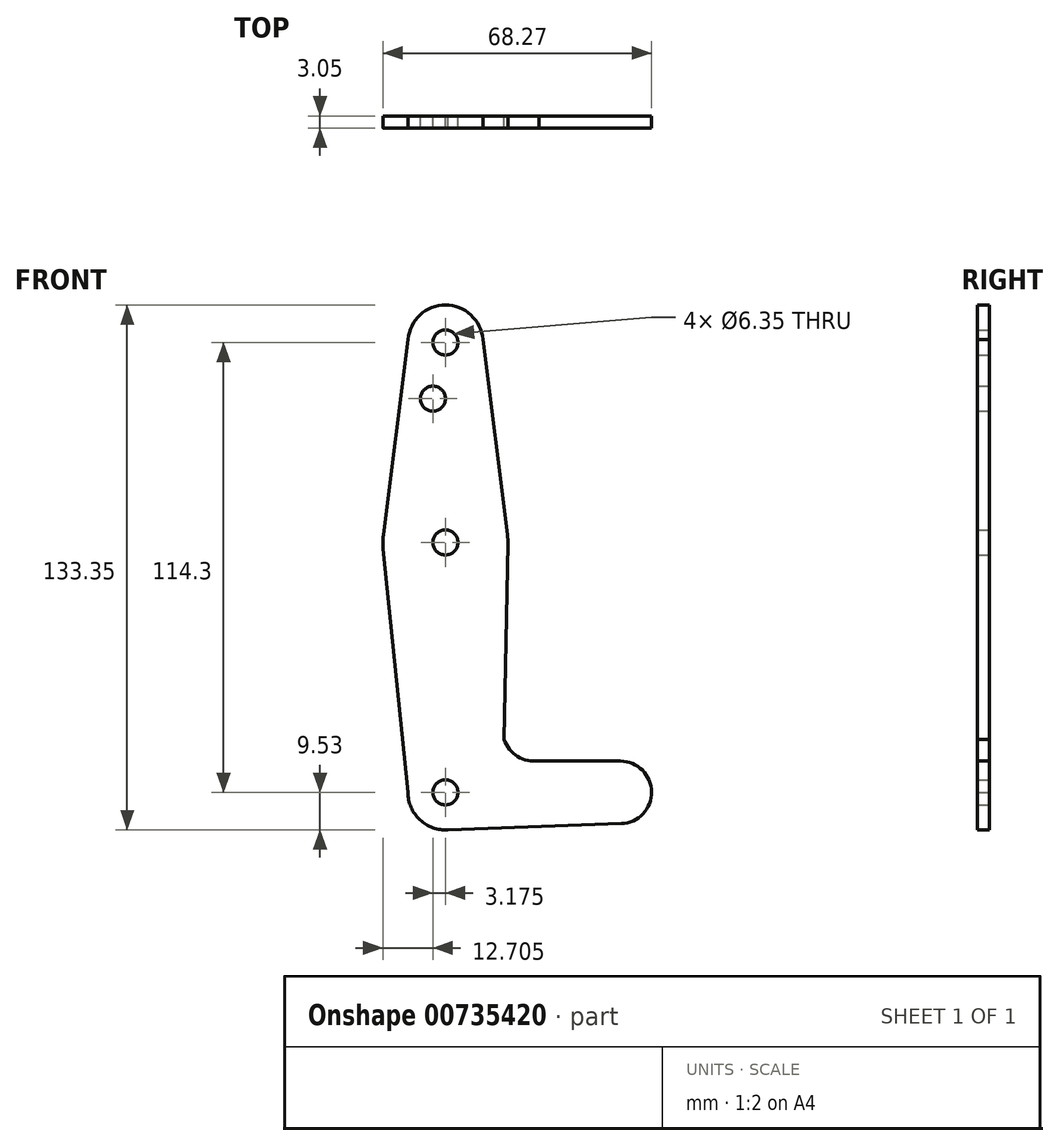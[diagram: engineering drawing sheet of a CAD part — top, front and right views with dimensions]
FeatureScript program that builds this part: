
annotation { "Feature Type Name" : "Feature", "Feature Type Description" : "" }
export const myFeature = defineFeature(function(context is Context, id is Id, definition is map)
    precondition{}
    {
        {
            var Q0;
            Q0=qCreatedBy(makeId("Front.planeOp"),FACE);
            var sketch = newSketch(context, id + "F0", { "sketchPlane" : qUnion([Q0])});
            skCircle(sketch, "E0", {"center": v(0, 0) * mm, "radius": 9.53 * mm});
            skLineSegment(sketch, "E1", {"start": v(0, 0) * mm, "end": v(0, 63.5) * mm});
            skCircle(sketch, "E2", {"center": v(0, 63.5) * mm, "radius": 15.88 * mm});
            skLineSegment(sketch, "E3", {"start": v(0, 63.5) * mm, "end": v(0, 114.3) * mm});
            skCircle(sketch, "E4", {"center": v(0, 114.3) * mm, "radius": 9.53 * mm});
            skLineSegment(sketch, "E5", {"start": v(0, 0) * mm, "end": v(44.45, 0) * mm});
            skCircle(sketch, "E6", {"center": v(44.45, 0) * mm, "radius": 7.94 * mm});
            skCircle(sketch, "E7", {"center": v(0, 114.3) * mm, "radius": 3.18 * mm});
            skCircle(sketch, "E8", {"center": v(0, 0) * mm, "radius": 3.18 * mm});
            skLineSegment(sketch, "E9", {"start": v(-9.4, 115.89) * mm, "end": v(-15.75, 65.49) * mm});
            skLineSegment(sketch, "E10", {"start": v(9.4, 115.89) * mm, "end": v(15.75, 65.49) * mm});
            skCircle(sketch, "E11", {"center": v(0, 63.5) * mm, "radius": 3.18 * mm});
            skCircle(sketch, "E12", {"center": v(-3.18, 100.03) * mm, "radius": 3.18 * mm});
            skLineSegment(sketch, "E13", {"start": v(0, -9.53) * mm, "end": v(44.73, -7.93) * mm});
            skLineSegment(sketch, "E14", {"start": v(15.87, 63.2) * mm, "end": v(14.94, 13.46) * mm});
            skArc(sketch, "E15", {"start": v(14.94, 13.46) * mm, "mid": v(18.36, 9.1) * mm, "end": v(23.8, 8.04) * mm});
            skLineSegment(sketch, "E16", {"start": v(23.8, 8.04) * mm, "end": v(44.49, 7.94) * mm});
            skLineSegment(sketch, "E17", {"start": v(-9.53, 0) * mm, "end": v(-15.8, 61.9) * mm});
            skSolve(sketch);
        }
        {
            var Q0;
            Q0 = qSketchRegion(id + "F0", true);
            var Q1;
            {var subQ0=sQuery(id+"F0.wireOp",EDGE,"E1");var subQ1=sQuery(id+"F0.wireOp",EDGE,"E0");var subQ2=makeQuery(id+"F0.imprint","INTERSECT",VERTEX,{"derivedFrom":[subQ1,subQ0]});Q1=makeQuery(id+"F0.imprint","IMPRINT",FACE,{"disambiguationData":[TD([[makeQuery(id+"F0.imprint","IMPRINT",EDGE,{"disambiguationData":[TD([[subQ2,1.0]])],"derivedFrom":subQ1}),1.0]])]});}
            extrude(context, id + "F1", {"entities" : qUnion([Q0, Q1]), "depth" : 3.05 * mm, "offsetDistance" : 25.4 * mm});
        }
    });
